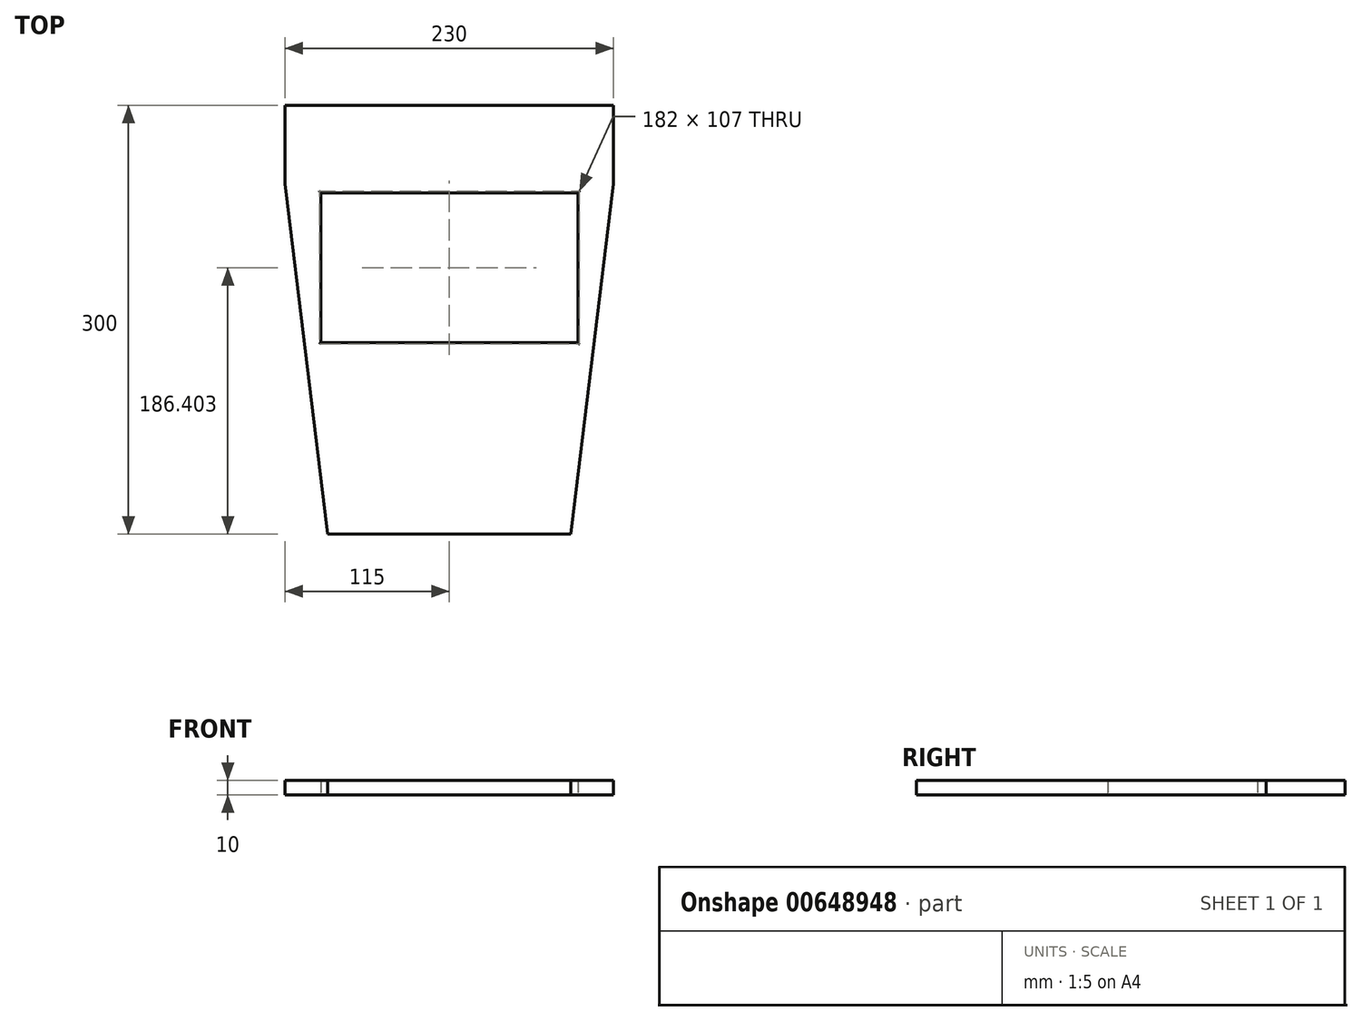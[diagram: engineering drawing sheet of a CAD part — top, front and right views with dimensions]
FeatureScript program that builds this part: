
annotation { "Feature Type Name" : "Feature", "Feature Type Description" : "" }
export const myFeature = defineFeature(function(context is Context, id is Id, definition is map)
    precondition{}
    {
        {
            var Q0;
            Q0=qCreatedBy(makeId("Top.planeOp"),FACE);
            var sketch = newSketch(context, id + "F0", { "sketchPlane" : qUnion([Q0])});
            skLineSegment(sketch, "E0.bottom", {"start": v(115, 115.05) * mm, "end": v(-115, 115.05) * mm});
            skLineSegment(sketch, "E0.top", {"start": v(115, 170.05) * mm, "end": v(-115, 170.05) * mm});
            skLineSegment(sketch, "E0.left", {"start": v(115, 115.05) * mm, "end": v(115, 170.05) * mm});
            skLineSegment(sketch, "E0.right", {"start": v(-115, 115.05) * mm, "end": v(-115, 170.05) * mm});
            skPoint(sketch, "E0.middle", {"position": v(0, 142.55) * mm});
            skLineSegment(sketch, "E1.bottom", {"start": v(85, -129.95) * mm, "end": v(-85, -129.95) * mm});
            skLineSegment(sketch, "E1.top", {"start": v(85, -109.95) * mm, "end": v(-85, -109.95) * mm});
            skLineSegment(sketch, "E1.left", {"start": v(85, -129.95) * mm, "end": v(85, -109.95) * mm});
            skLineSegment(sketch, "E1.right", {"start": v(-85, -129.95) * mm, "end": v(-85, -109.95) * mm});
            skPoint(sketch, "E1.middle", {"position": v(0, -119.95) * mm});
            skLineSegment(sketch, "E2", {"start": v(115, 115.05) * mm, "end": v(85, -129.95) * mm});
            skLineSegment(sketch, "E3", {"start": v(-115, 115.05) * mm, "end": v(-85, -129.95) * mm});
            skLineSegment(sketch, "E4.bottom", {"start": v(90, 108.95) * mm, "end": v(-90, 108.95) * mm});
            skLineSegment(sketch, "E4.top", {"start": v(90, 3.95) * mm, "end": v(-90, 3.95) * mm});
            skLineSegment(sketch, "E4.left", {"start": v(90, 108.95) * mm, "end": v(90, 3.95) * mm});
            skLineSegment(sketch, "E4.right", {"start": v(-90, 108.95) * mm, "end": v(-90, 3.95) * mm});
            skPoint(sketch, "E4.middle", {"position": v(0, 56.45) * mm});
            skSolve(sketch);
        }
        {
            var Q0;
            Q0=qSketchRegion(id+"F0",true);
            extrude(context, id + "F1", {"entities" : qUnion([Q0]), "depth" : 10 * mm, "offsetDistance" : 25 * mm});
        }
        {
            var Q0;
            Q0=makeQuery(id+"F1.opExtrude","CAP_EDGE",EDGE,{"disambiguationData":[OSD([sQuery(id+"F0.wireOp",EDGE,"E4.bottom")])],"isStart":true});
            var Q1;
            Q1=makeQuery(id+"F1.opExtrude","CAP_EDGE",EDGE,{"disambiguationData":[OSD([sQuery(id+"F0.wireOp",EDGE,"E4.left")])],"isStart":false});
            var Q2;
            Q2=makeQuery(id+"F1.opExtrude","CAP_EDGE",EDGE,{"disambiguationData":[OSD([sQuery(id+"F0.wireOp",EDGE,"E4.top")])],"isStart":false});
            var Q3;
            Q3=makeQuery(id+"F1.opExtrude","CAP_EDGE",EDGE,{"disambiguationData":[OSD([sQuery(id+"F0.wireOp",EDGE,"E4.right")])],"isStart":false});
            var Q4;
            Q4=makeQuery(id+"F1.opExtrude","CAP_EDGE",EDGE,{"disambiguationData":[OSD([sQuery(id+"F0.wireOp",EDGE,"E4.top")])],"isStart":true});
            var Q5;
            Q5=makeQuery(id+"F1.opExtrude","CAP_EDGE",EDGE,{"disambiguationData":[OSD([sQuery(id+"F0.wireOp",EDGE,"E4.right")])],"isStart":true});
            var Q6;
            Q6=makeQuery(id+"F1.opExtrude","CAP_EDGE",EDGE,{"disambiguationData":[OSD([sQuery(id+"F0.wireOp",EDGE,"E4.bottom")])],"isStart":false});
            var Q7;
            Q7=makeQuery(id+"F1.opExtrude","CAP_EDGE",EDGE,{"disambiguationData":[OSD([sQuery(id+"F0.wireOp",EDGE,"E4.left")])],"isStart":true});
            fillet(context, id + "F2", {"entities" : qUnion([Q0, Q1, Q2, Q3, Q4, Q5, Q6, Q7]), "radius" : 1 * mm, "tangentPropagation" : true, "allowEdgeOverflow" : false});
        }
    });
